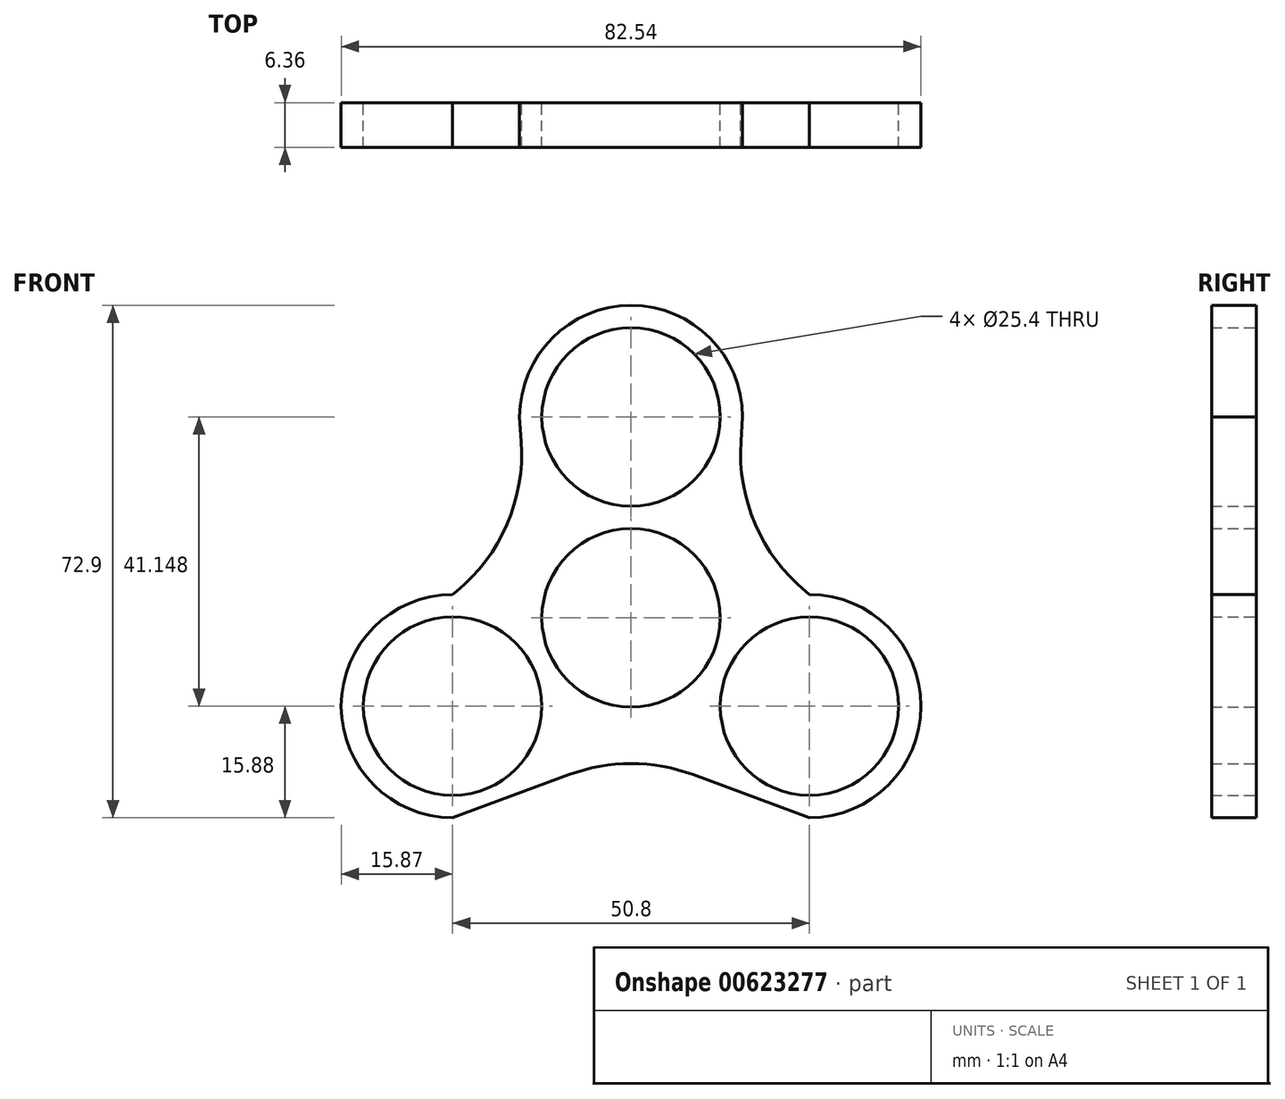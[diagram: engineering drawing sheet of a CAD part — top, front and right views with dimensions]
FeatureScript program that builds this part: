
annotation { "Feature Type Name" : "Feature", "Feature Type Description" : "" }
export const myFeature = defineFeature(function(context is Context, id is Id, definition is map)
    precondition{}
    {
        {
            var Q0;
            Q0=qCreatedBy(makeId("Front.planeOp"),FACE);
            var sketch = newSketch(context, id + "F0", { "sketchPlane" : qUnion([Q0])});
            skCircle(sketch, "E0", {"center": v(-25.4, 0) * mm, "radius": 12.7 * mm});
            skCircle(sketch, "E1", {"center": v(25.4, 0) * mm, "radius": 12.7 * mm});
            skCircle(sketch, "E2", {"center": v(0, 41.15) * mm, "radius": 12.7 * mm});
            skArc(sketch, "E3", {"start": v(-25.4, -15.88) * mm, "mid": v(-36.63, -11.23) * mm, "end": v(-41.28, 0) * mm});
            skArc(sketch, "E4.MirrorCS", {"start": v(25.4, -15.88) * mm, "mid": v(36.63, -11.23) * mm, "end": v(41.28, 0) * mm});
            skArc(sketch, "E5.MirrorCS", {"start": v(-25.4, 15.88) * mm, "mid": v(-36.63, 11.23) * mm, "end": v(-41.28, 0) * mm});
            skArc(sketch, "E6.MirrorCS", {"start": v(25.4, 15.88) * mm, "mid": v(36.63, 11.23) * mm, "end": v(41.28, 0) * mm});
            skArc(sketch, "E7", {"start": v(0, 57.02) * mm, "mid": v(-11.23, 52.37) * mm, "end": v(-15.88, 41.15) * mm});
            skArc(sketch, "E8.MirrorCS", {"start": v(0, 57.02) * mm, "mid": v(11.23, 52.37) * mm, "end": v(15.88, 41.15) * mm});
            skCircle(sketch, "E9", {"center": v(0, 12.57) * mm, "radius": 12.7 * mm});
            skLineSegment(sketch, "E10", {"start": v(-25.4, -15.88) * mm, "end": v(-8.81, -9.74) * mm});
            skLineSegment(sketch, "E11", {"start": v(8.81, -9.74) * mm, "end": v(25.4, -15.88) * mm});
            skPoint(sketch, "E12.visualSharp", {"position": v(0, -6.48) * mm});
            skArc(sketch, "E12.filletArc", {"start": v(8.81, -9.74) * mm, "mid": v(0, -8.16) * mm, "end": v(-8.81, -9.74) * mm});
            skLineSegment(sketch, "E13", {"start": v(-25.4, 15.88) * mm, "end": v(-24.86, 16.32) * mm});
            skLineSegment(sketch, "E14", {"start": v(-15.88, 41.15) * mm, "end": v(-15.64, 37.65) * mm});
            skLineSegment(sketch, "E15.MirrorCS", {"start": v(15.88, 41.15) * mm, "end": v(15.64, 37.65) * mm});
            skLineSegment(sketch, "E16.MirrorCS", {"start": v(25.4, 15.88) * mm, "end": v(24.86, 16.32) * mm});
            skPoint(sketch, "E17.visualSharp", {"position": v(-14.76, 24.61) * mm});
            skArc(sketch, "E17.filletArc", {"start": v(-24.86, 16.32) * mm, "mid": v(-17.67, 25.87) * mm, "end": v(-15.64, 37.65) * mm});
            skPoint(sketch, "E18.visualSharp", {"position": v(14.76, 24.61) * mm});
            skArc(sketch, "E18.filletArc", {"start": v(15.64, 37.65) * mm, "mid": v(17.67, 25.87) * mm, "end": v(24.86, 16.32) * mm});
            skSolve(sketch);
        }
        {
            var Q0;
            Q0 = qSketchRegion(id + "F0", true);
            extrude(context, id + "F1", {"entities" : qUnion([Q0]), "endBound" : BoundingType.SYMMETRIC, "depth" : 6.35 * mm, "offsetDistance" : 25.4 * mm});
        }
    });
